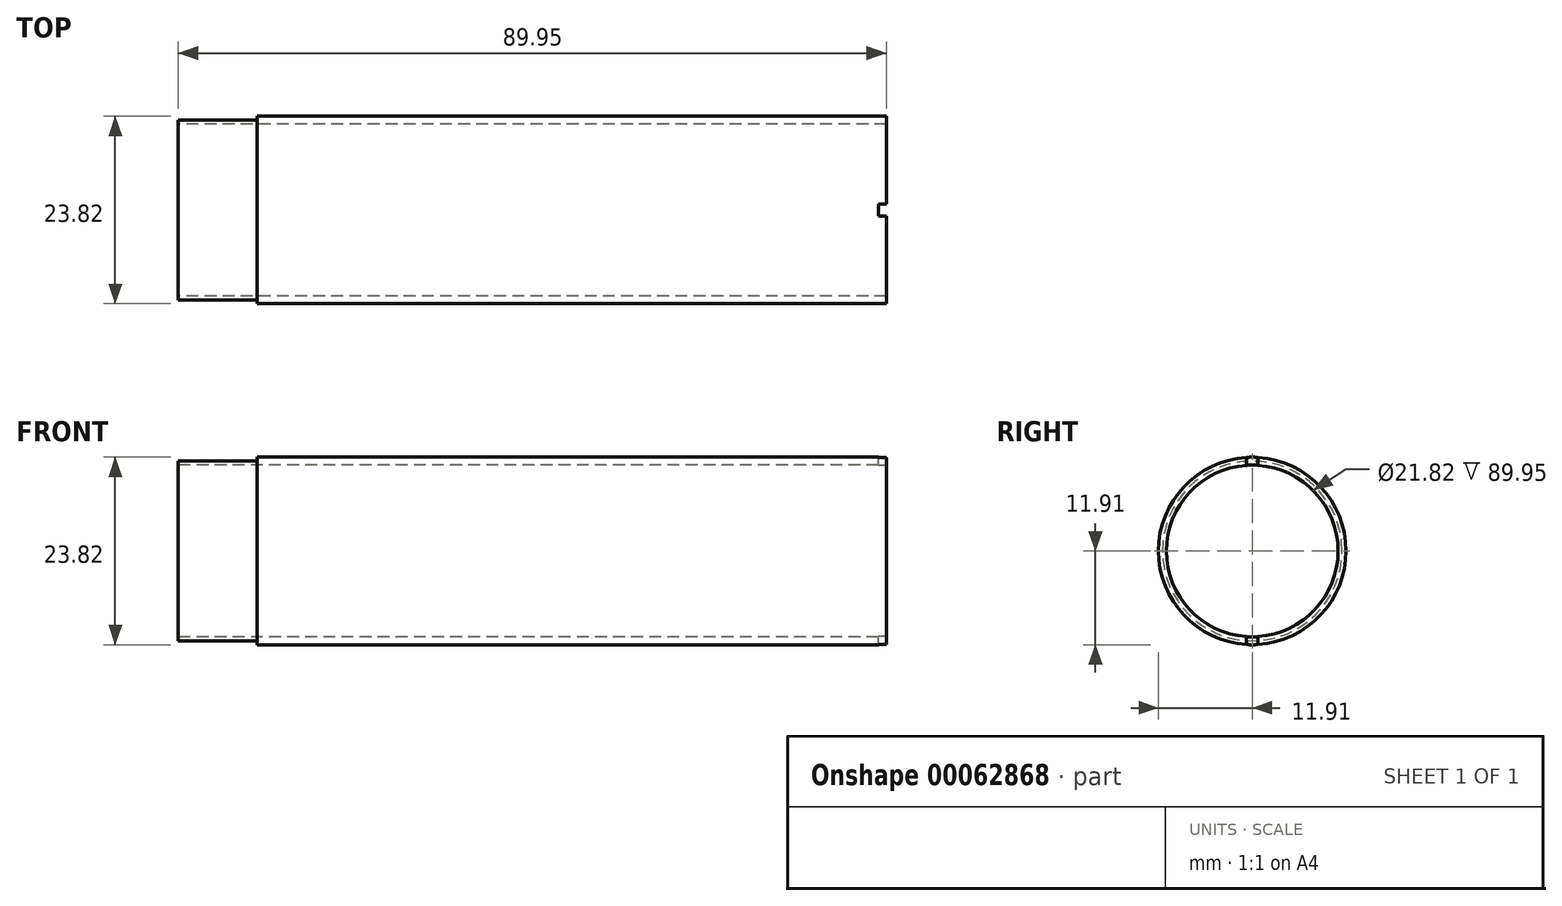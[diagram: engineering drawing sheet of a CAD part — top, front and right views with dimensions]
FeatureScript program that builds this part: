
annotation { "Feature Type Name" : "Feature", "Feature Type Description" : "" }
export const myFeature = defineFeature(function(context is Context, id is Id, definition is map)
    precondition{}
    {
        {
            var Q0;
            Q0=qCreatedBy(makeId("Front.planeOp"),FACE);
            var sketch = newSketch(context, id + "F0", { "sketchPlane" : qUnion([Q0])});
            skLineSegment(sketch, "E0", {"start": v(-31.35, 11.91) * mm, "end": v(48.6, 11.91) * mm});
            skLineSegment(sketch, "E1", {"start": v(-31.35, 11.91) * mm, "end": v(-31.35, 11.41) * mm});
            skLineSegment(sketch, "E2", {"start": v(-31.35, 11.41) * mm, "end": v(-41.35, 11.41) * mm});
            skLineSegment(sketch, "E3", {"start": v(-41.35, 11.41) * mm, "end": v(-41.35, 10.91) * mm});
            skLineSegment(sketch, "E4", {"start": v(48.6, 11.91) * mm, "end": v(48.6, 10.91) * mm});
            skLineSegment(sketch, "E5", {"start": v(48.6, 10.91) * mm, "end": v(-41.35, 10.91) * mm});
            skLineSegment(sketch, "E6", {"start": v(-31.35, 11.91) * mm, "end": v(-31.35, 0) * mm});
            skLineSegment(sketch, "E7", {"start": v(-31.35, 0) * mm, "end": v(-12.5, 0) * mm});
            skSolve(sketch);
        }
        {
            var Q0;
            Q0 = qSketchRegion(id + "F0", true);
            var Q1;
            Q1=sQuery(id+"F0.wireOp",EDGE,"E7");
            revolve(context, id + "F1", {"entities" : qUnion([Q0]), "axis" : qUnion([Q1]), "revolveType" : RevolveType.FULL});
        }
        {
            var Q0;
            Q0=qCreatedBy(makeId("Top.planeOp"),FACE);
            var sketch = newSketch(context, id + "F2", { "sketchPlane" : qUnion([Q0])});
            skLineSegment(sketch, "E8", {"start": v(0, 0) * mm, "end": v(48.59, 0) * mm});
            skLineSegment(sketch, "E9.rect.bottom", {"start": v(49.59, 0.75) * mm, "end": v(47.59, 0.75) * mm});
            skLineSegment(sketch, "E9.rect.top", {"start": v(49.59, -0.75) * mm, "end": v(47.59, -0.75) * mm});
            skLineSegment(sketch, "E9.rect.left", {"start": v(49.59, 0.75) * mm, "end": v(49.59, -0.75) * mm});
            skLineSegment(sketch, "E9.rect.right", {"start": v(47.59, 0.75) * mm, "end": v(47.59, -0.75) * mm});
            skPoint(sketch, "E9.rect.middle", {"position": v(48.59, 0) * mm});
            skSolve(sketch);
        }
        {
            var Q0;
            {var subQ0=sQuery(id+"F2.wireOp",EDGE,"E9.rect.bottom");Q0=makeQuery(id+"F2.imprint","IMPRINT",FACE,{"disambiguationData":[TD([[makeQuery(id+"F2.imprint","IMPRINT",EDGE,{"derivedFrom":subQ0}),1.0]])]});}
            extrude(context, id + "F3", {"entities" : qUnion([Q0]), "operationType" : NewBodyOperationType.REMOVE, "endBound" : BoundingType.SYMMETRIC, "oppositeDirection" : true, "depth" : 25 * mm});
        }
    });
